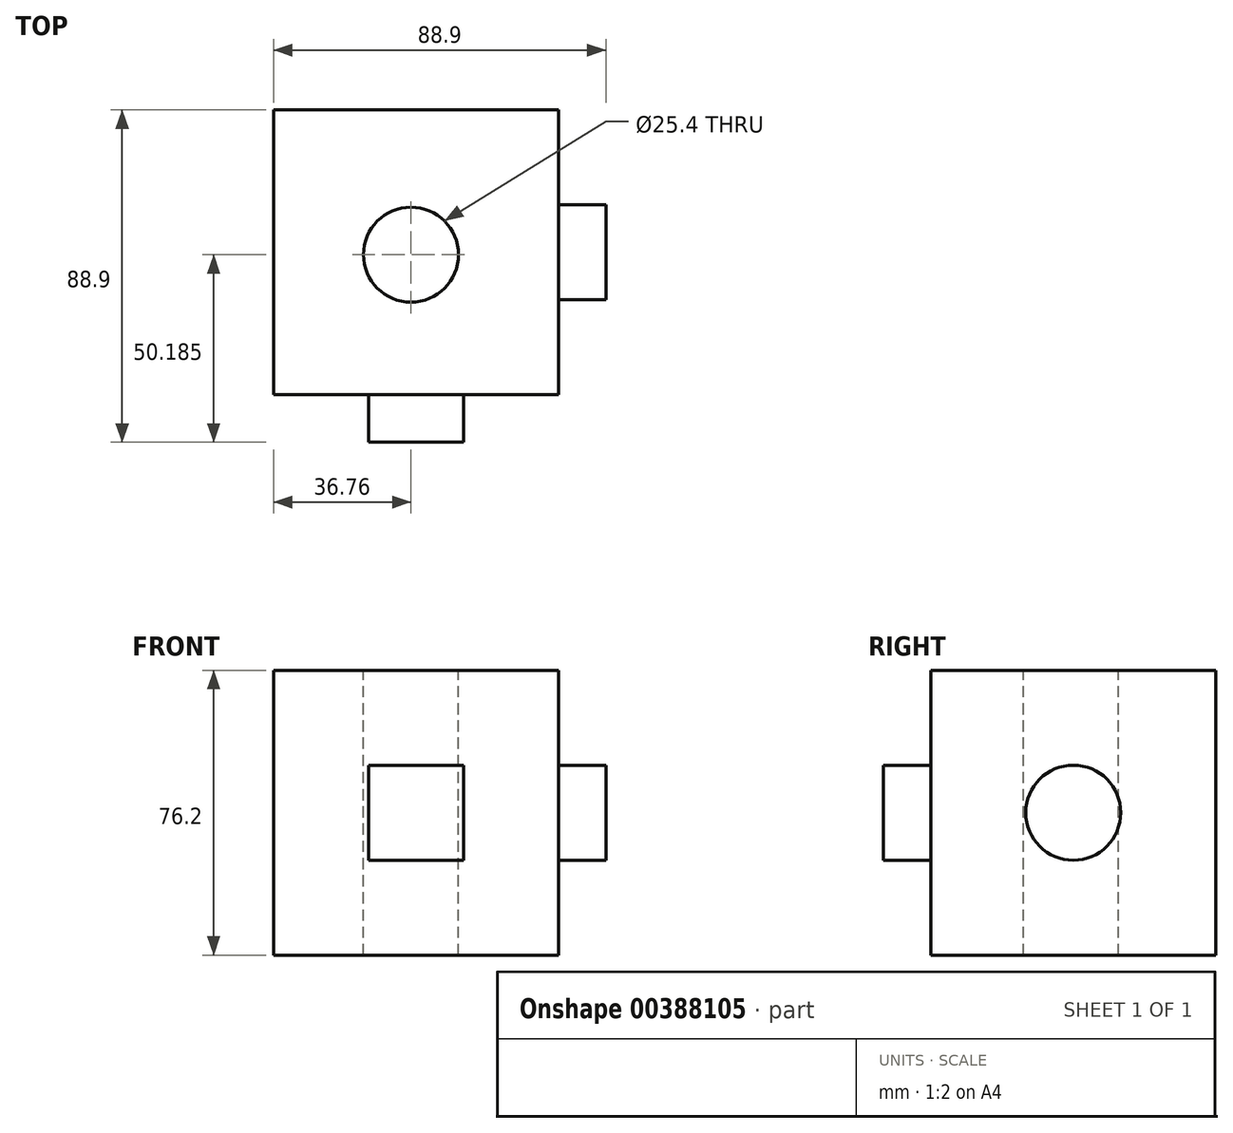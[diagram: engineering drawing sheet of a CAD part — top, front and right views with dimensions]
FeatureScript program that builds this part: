
annotation { "Feature Type Name" : "Feature", "Feature Type Description" : "" }
export const myFeature = defineFeature(function(context is Context, id is Id, definition is map)
    precondition{}
    {
        {
            var Q0;
            Q0=qCreatedBy(makeId("Front.planeOp"),FACE);
            var sketch = newSketch(context, id + "F0", { "sketchPlane" : qUnion([Q0])});
            skLineSegment(sketch, "E0.bottom", {"start": v(-36.76, 47.42) * mm, "end": v(39.44, 47.42) * mm});
            skLineSegment(sketch, "E0.top", {"start": v(-36.76, -28.78) * mm, "end": v(39.44, -28.78) * mm});
            skLineSegment(sketch, "E0.left", {"start": v(-36.76, 47.42) * mm, "end": v(-36.76, -28.78) * mm});
            skLineSegment(sketch, "E0.right", {"start": v(39.44, 47.42) * mm, "end": v(39.44, -28.78) * mm});
            skSolve(sketch);
        }
        {
            var Q0;
            Q0=makeQuery(id+"F0.imprint","IMPRINT",FACE,{"disambiguationData":[TD([[makeQuery(id+"F0.imprint","IMPRINT",EDGE,{"derivedFrom":sQuery(id+"F0.wireOp",EDGE,"E0.bottom")}),-1.0]])]});
            extrude(context, id + "F1", {"entities" : qUnion([Q0]), "depth" : 76.2 * mm});
        }
        {
            var Q0;
            Q0=makeQuery(id+"F1.opExtrude","SWEPT_FACE",FACE,{"disambiguationData":[OSD([sQuery(id+"F0.wireOp",EDGE,"E0.bottom")])]});
            var sketch = newSketch(context, id + "F2", { "sketchPlane" : qUnion([Q0])});
            skPoint(sketch, "E1", {"position": v(0, -38.71) * mm});
            skSolve(sketch);
        }
        {
            var Q0;
            Q0=sQuery(id+"F2.wireOp",VERTEX,"E1");
            var Q1;
            Q1=makeQuery(id+"F1.opExtrude","SWEPT_BODY",BODY,{"disambiguationData":[OSD([sQuery(id+"F0.wireOp",EDGE,"E0.bottom"),sQuery(id+"F0.wireOp",EDGE,"E0.top"),sQuery(id+"F0.wireOp",EDGE,"E0.left"),sQuery(id+"F0.wireOp",EDGE,"E0.right")])]});
            hole(context, id + "F3", {"style" : HoleStyle.SIMPLE, "endStyle" : HoleEndStyle.THROUGH, "holeDiameter" : 25.4 * mm, "isTappedThrough" : true, "tappedDepth" : 12.7 * mm, "tapClearance" : 3, "locations" : qUnion([Q0]), "scope" : qUnion([Q1])});
        }
        {
            var Q0;
            Q0=makeQuery(id+"F1.opExtrude","CAP_FACE",FACE,{"disambiguationData":[OSD([sQuery(id+"F0.wireOp",EDGE,"E0.bottom"),sQuery(id+"F0.wireOp",EDGE,"E0.top"),sQuery(id+"F0.wireOp",EDGE,"E0.left"),sQuery(id+"F0.wireOp",EDGE,"E0.right")])],"isStart":false});
            var sketch = newSketch(context, id + "F4", { "sketchPlane" : qUnion([Q0])});
            skLineSegment(sketch, "E2.bottom", {"start": v(-11.36, 22.02) * mm, "end": v(14.04, 22.02) * mm});
            skLineSegment(sketch, "E2.top", {"start": v(-11.36, -3.38) * mm, "end": v(14.04, -3.38) * mm});
            skLineSegment(sketch, "E2.left", {"start": v(-11.36, 22.02) * mm, "end": v(-11.36, -3.38) * mm});
            skLineSegment(sketch, "E2.right", {"start": v(14.04, 22.02) * mm, "end": v(14.04, -3.38) * mm});
            skSolve(sketch);
        }
        {
            var Q0;
            Q0 = qSketchRegion(id + "F4", true);
            extrude(context, id + "F5", {"entities" : qUnion([Q0]), "operationType" : NewBodyOperationType.ADD, "depth" : 12.7 * mm});
        }
        {
            var Q0;
            Q0=makeQuery(id+"F1.opExtrude","SWEPT_FACE",FACE,{"disambiguationData":[OSD([sQuery(id+"F0.wireOp",EDGE,"E0.right")])]});
            var sketch = newSketch(context, id + "F6", { "sketchPlane" : qUnion([Q0])});
            skPoint(sketch, "E3", {"position": v(-38.1, 9.32) * mm});
            skCircle(sketch, "E4", {"center": v(-38.1, 9.32) * mm, "radius": 12.7 * mm});
            skSolve(sketch);
        }
        {
            var Q0;
            Q0=makeQuery(id+"F6.imprint","IMPRINT",FACE,{"disambiguationData":[TD([[makeQuery(id+"F6.imprint","IMPRINT",EDGE,{"derivedFrom":sQuery(id+"F6.wireOp",EDGE,"E4")}),1.0]])]});
            extrude(context, id + "F7", {"entities" : qUnion([Q0]), "operationType" : NewBodyOperationType.ADD, "depth" : 12.7 * mm});
        }
    });
